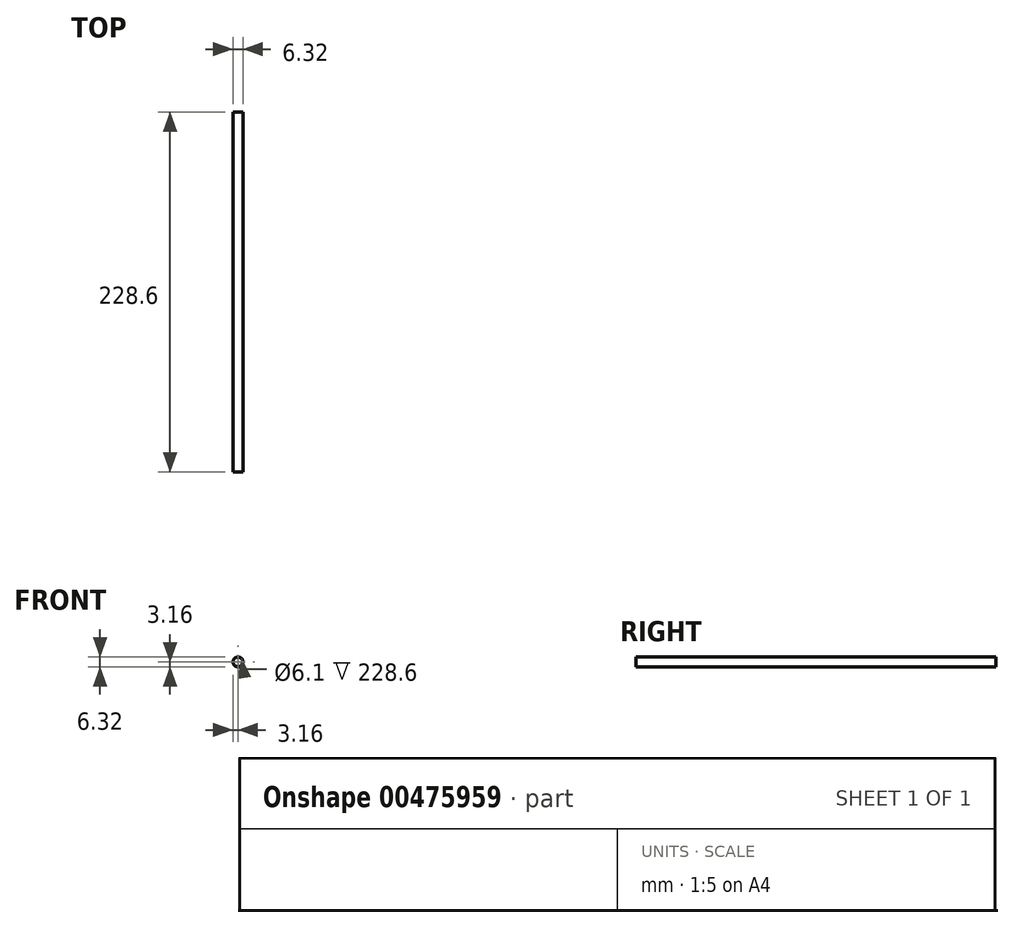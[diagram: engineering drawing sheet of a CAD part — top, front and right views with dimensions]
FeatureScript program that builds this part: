
annotation { "Feature Type Name" : "Feature", "Feature Type Description" : "" }
export const myFeature = defineFeature(function(context is Context, id is Id, definition is map)
    precondition{}
    {
        {
            var Q0;
            Q0=qCreatedBy(makeId("Front.planeOp"),FACE);
            var sketch = newSketch(context, id + "F0", { "sketchPlane" : qUnion([Q0])});
            skCircle(sketch, "E0", {"center": v(0, 0) * mm, "radius": 3.05 * mm});
            skCircle(sketch, "E1", {"center": v(0, 0) * mm, "radius": 3.16 * mm});
            skSolve(sketch);
        }
        {
            var Q0;
            Q0 = qSketchRegion(id + "F0", true);
            extrude(context, id + "F1", {"entities" : qUnion([Q0]), "depth" : 228.6 * mm, "offsetDistance" : 25.4 * mm});
        }
    });
